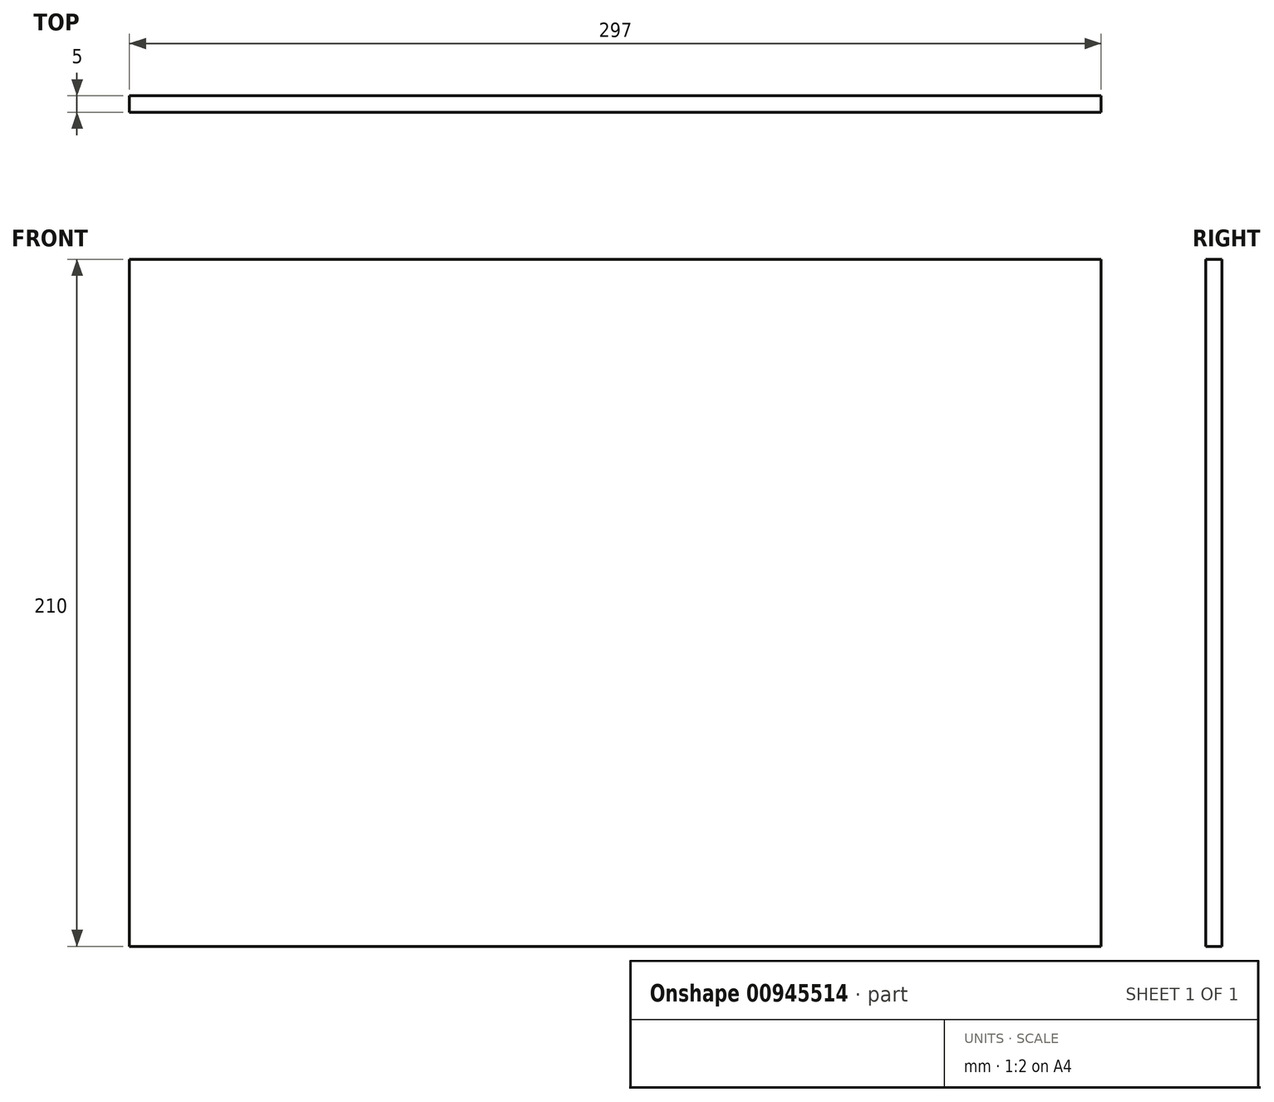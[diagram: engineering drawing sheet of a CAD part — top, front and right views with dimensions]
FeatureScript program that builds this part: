
annotation { "Feature Type Name" : "Feature", "Feature Type Description" : "" }
export const myFeature = defineFeature(function(context is Context, id is Id, definition is map)
    precondition{}
    {
        {
            var Q0;
            Q0=qCreatedBy(makeId("Front.planeOp"),FACE);
            var sketch = newSketch(context, id + "F0", { "sketchPlane" : qUnion([Q0])});
            skLineSegment(sketch, "E0.bottom", {"start": v(148.5, 105) * mm, "end": v(-148.5, 105) * mm});
            skLineSegment(sketch, "E0.top", {"start": v(148.5, -105) * mm, "end": v(-148.5, -105) * mm});
            skLineSegment(sketch, "E0.left", {"start": v(148.5, 105) * mm, "end": v(148.5, -105) * mm});
            skLineSegment(sketch, "E0.right", {"start": v(-148.5, 105) * mm, "end": v(-148.5, -105) * mm});
            skPoint(sketch, "E0.middle", {"position": v(0, 0) * mm});
            skSolve(sketch);
        }
        {
            var Q0;
            Q0=makeQuery(id+"F0.imprint","IMPRINT",FACE,{"disambiguationData":[TD([[makeQuery(id+"F0.imprint","IMPRINT",EDGE,{"derivedFrom":sQuery(id+"F0.wireOp",EDGE,"E0.bottom")}),1.0]])]});
            extrude(context, id + "F1", {"entities" : qUnion([Q0]), "depth" : 5 * mm, "offsetDistance" : 25 * mm});
        }
    });
